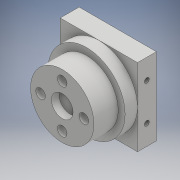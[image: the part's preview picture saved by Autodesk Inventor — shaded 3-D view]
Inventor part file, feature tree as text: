
AUTODESK INVENTOR PART (.ipt)
format: ipt  version: 2018 (Build 220112000, 112)  size: 195,584 bytes
history: native  units: mm
features: sketch x7, extrude x4, hole x3, projected_geometry x3
ambient origin geometry x8: Origin, YZ Plane, XZ Plane, XY Plane, X Axis, Y Axis, Z Axis, Center Point
bodies: Solid1 (feature_tree)
feature tree (17):
  extrude  "Extrusion1"  Depth=7.85mm TaperAngle=0.0deg
  extrude  "Extrusion2"  Depth=4.0mm TaperAngle=0.0deg
  extrude  "Extrusion3"  Depth=25.0mm
  hole  "Hole1"  [1 undecoded]
  extrude  "Extrusion4"  Depth=7.0mm
  hole  "Hole2"  [1 undecoded]
  hole  "Hole3"  [1 undecoded]
  sketch  "Sketch1"  dims[d0=20.5mm d1=7.85mm d2=0.0mm]
  sketch  "Sketch2"  dims[d3=24.95mm d4=4.0mm d5=0.0mm]
  sketch  "Sketch3"  dims[d6=25.0mm d7=25.0mm]
  projected_geometry  "Projected Loop1"
  sketch  "Sketch4"  dims[d8=6.1mm d9=0.0mm d10=12.0mm]
  projected_geometry  "Projected Loop2"
  sketch  "Sketch5"  dims[d11=3.0mm]
  sketch  "Sketch6"  dims[d12=1.567mm d13=25.0mm d14=4.0mm d15=2.0mm d16=90.0deg d17=6.3mm d18=20.594885mm d19=7.0mm]
  sketch  "Sketch7"  dims[d20=2.5mm d21=0.0mm d22=14.0mm d23=3.1mm d24=25.0mm d25=6.3mm d26=2.0mm d27=90.0deg d28=6.3mm d29=20.594885mm d30=5.7mm d31=25.0mm d32=6.3mm d33=2.0mm d34=90.0deg d35=3.2mm d36=17.453293mm]
  projected_geometry  "Projected Loop3"
note: 3 required parameter values undecoded (feature->parameter linkage not recoverable at this tier; creation-order binding heuristic only, values carry confidence <= 0.55)
